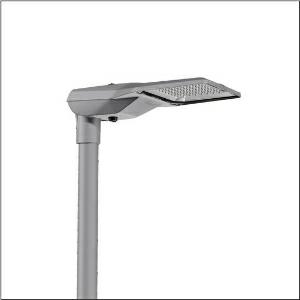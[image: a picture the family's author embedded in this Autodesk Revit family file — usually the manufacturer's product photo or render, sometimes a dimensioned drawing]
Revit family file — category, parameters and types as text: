
# Revit family: streetlight_sl_21_midi___stw1_0a_5xe3e63t08lb_15d1
name_source: partatom
category: Lighting Fixtures
units: mm (PartAtom-declared; Revit-internal decimal feet)

## family parameters
Cut with Voids When Loaded = No
Host = Face
Light Source = No
Part Type = Normal
Room Calculation Point = No
Round Connector Dimension = Use Diameter
Shared = No

## types (1)
- --- (1 x LED, 12860 lm, 99.6 W, 2700K)
    Apparent Load = 100 VA
    CIE Flux Codes = 38 75 98 100 100
    Color Rendering = 70
    Color Temperature = 2700K
    Default Elevation = 1800 mm
    Description = Streetlight SL 21 midi, mast luminaire, primary light control with lens, of PMMA, primary optical cover: cover, of toughened safety glass, transparent, light distribution: STW1.0a, light emission: direct distribution, primary light characteristic: asymmetric, installation type: side-entry, post-top, LED, High Power LED, rated luminous flux: 12.860lm, luminous efficacy: 129lm/W, light colour: 727, colour temperature: 2700K, control gear: D4i, control: overheat protection, constant luminous flux control, time-dependent luminous flux control, flexible luminous flux parameterisation, pre-setting: logarithmic dimming characteristic, mains connection: 230..240V, AC, 50/60Hz, start of lifetime: 100W, end of service life: 102W, reduction: 45W, luminaire housing, of diecast aluminium, powder-coated, Siteco® metallic grey (DB 702S), corrosivity category C5 mid according to DIN EN ISO 12944, please order mast flange separately, inclination adjustable: 0°, 5°, 10°, 15°, sealing non-destructively replaceable, multi-level sealing system, length: 644mm, width: 335mm, height: 110mm, mast flange for spigot size: 42mm (side-entry): 5XC10008XM4, 60/48mm (side-entry/post-top): 5XC10108XM2, 76/60mm (side-entry/post-top): 5XC10108XM1, mounting height: 4..8m, Smart Interface below and above, protection rating (complete): IP66, insulation class (complete): insulation class II (safety insulation), certification: CE, ENEC, ENEC+, VDE, impact resistance: IK10, permissible operating ambient temperature for outdoor applications: -40..+50°C, standard-compliant lighting for roads and squares, packaging unit: 1 piece

Light Distribution: STW1.0a
    Height = 111 mm
    Lamp = 1 x LED
    Lamp Light Flux = 12860 lm
    Lamp Power = 99.6 W
    Lamp count = 1
    Length = 644 mm
    Luminous efficacy = 129 lm/W
    Manufacturer = Siteco
    ModVariant = No
    Model = 5XE3E63T08LB
    Number of Poles = 1
    OnlyDefault = Yes
    Power Factor = 1
    Product Name = Streetlight SL 21 midi | STW1.0a
    Product group = mast luminaire | pylon top
    ProductGroupID = 6100
    Protection Class = Protection class II
    Protection Degree = IP 66
    RLX_Detail_Level = 1
    RLX_Emergency_Light_Flux = 0 lm
    RLX_Emergency_Type = 0
    RLX_Emergency_Type_DB = No
    RlxData = <blob elided: 26997 chars, md5=4e49d21d>
    Socket = socket
    Standby Power = 0 W
    System Light Flux = 12860 lm
    System Power = 100 W
    Type Comments = factory setting: luminous flux: 100 % | dim-lin: 254 | 1020 mA
    Type Image = l_1004304.jpg
    URL = http://relux.com
    VarID = @adj_011909
    Voltage = 0 V
    Weight = 0.00 kg
    Width = 336 mm

## geometry (parser evidence)
native form markers: Blend x4, Sweep x10
no freeform markers — native parametric forms only
